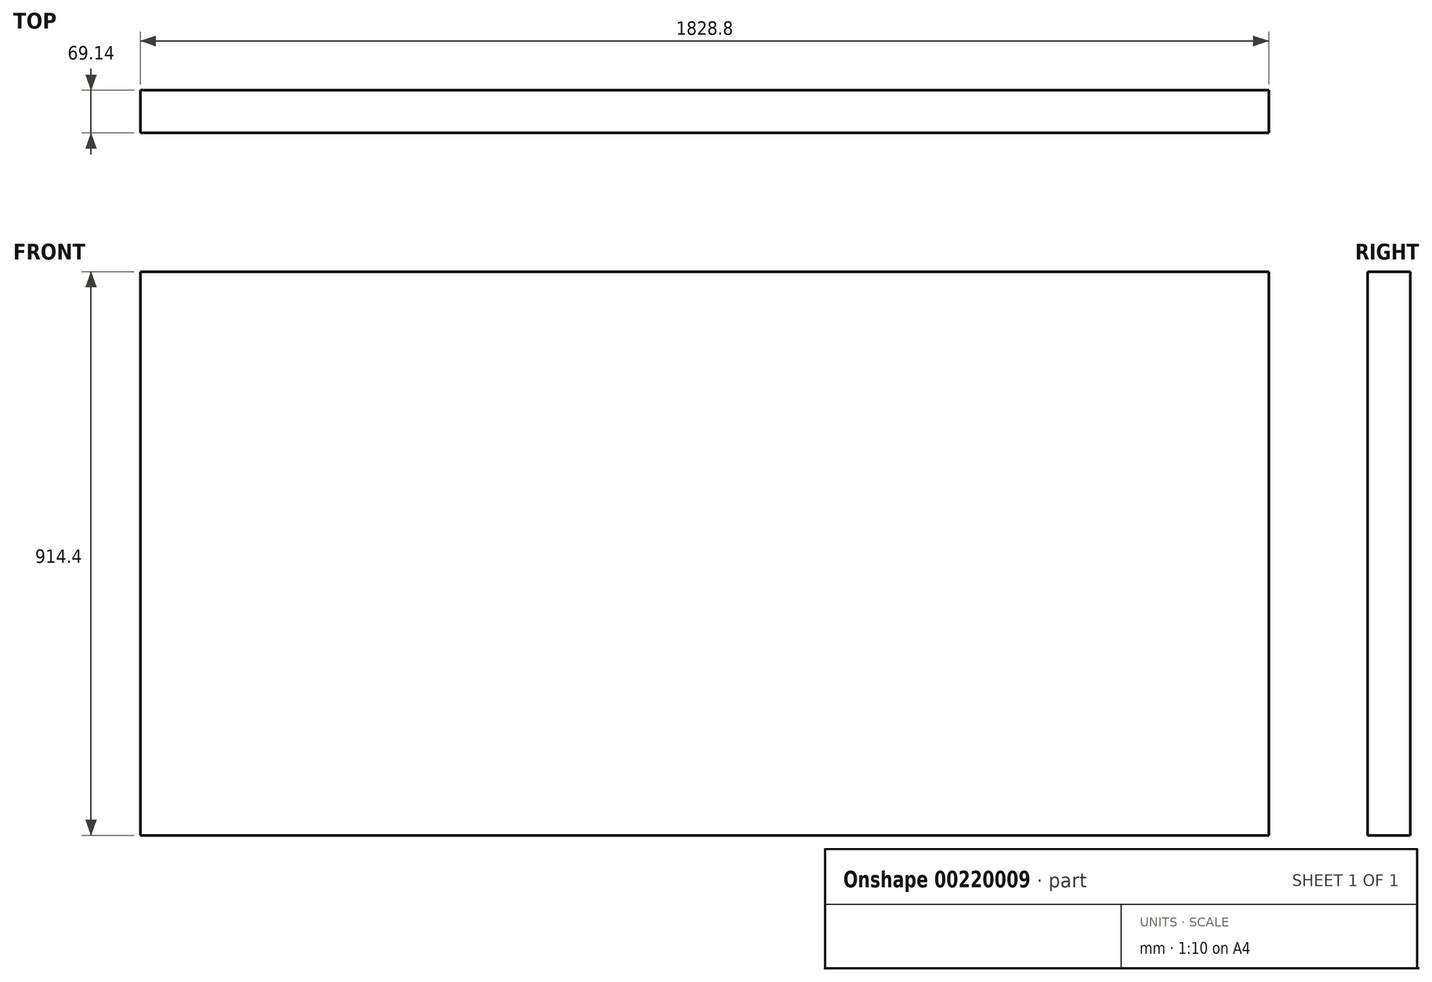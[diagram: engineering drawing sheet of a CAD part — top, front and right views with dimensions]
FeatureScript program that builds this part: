
annotation { "Feature Type Name" : "Feature", "Feature Type Description" : "" }
export const myFeature = defineFeature(function(context is Context, id is Id, definition is map)
    precondition{}
    {
        {
            var Q0;
            Q0=qCreatedBy(makeId("Front.planeOp"),FACE);
            var sketch = newSketch(context, id + "F0", { "sketchPlane" : qUnion([Q0])});
            skLineSegment(sketch, "E0.bottom", {"start": v(0, 0) * mm, "end": v(-1828.8, 0) * mm});
            skLineSegment(sketch, "E0.top", {"start": v(0, 914.4) * mm, "end": v(-1828.8, 914.4) * mm});
            skLineSegment(sketch, "E0.left", {"start": v(0, 0) * mm, "end": v(0, 914.4) * mm});
            skLineSegment(sketch, "E0.right", {"start": v(-1828.8, 0) * mm, "end": v(-1828.8, 914.4) * mm});
            skSolve(sketch);
        }
        {
            var Q0;
            Q0=makeQuery(id+"F0.imprint","IMPRINT",FACE,{"disambiguationData":[TD([[makeQuery(id+"F0.imprint","IMPRINT",EDGE,{"derivedFrom":sQuery(id+"F0.wireOp",EDGE,"E0.bottom")}),-1.0]])]});
            extrude(context, id + "F1", {"entities" : qUnion([Q0]), "depth" : 69.14 * mm});
        }
    });
